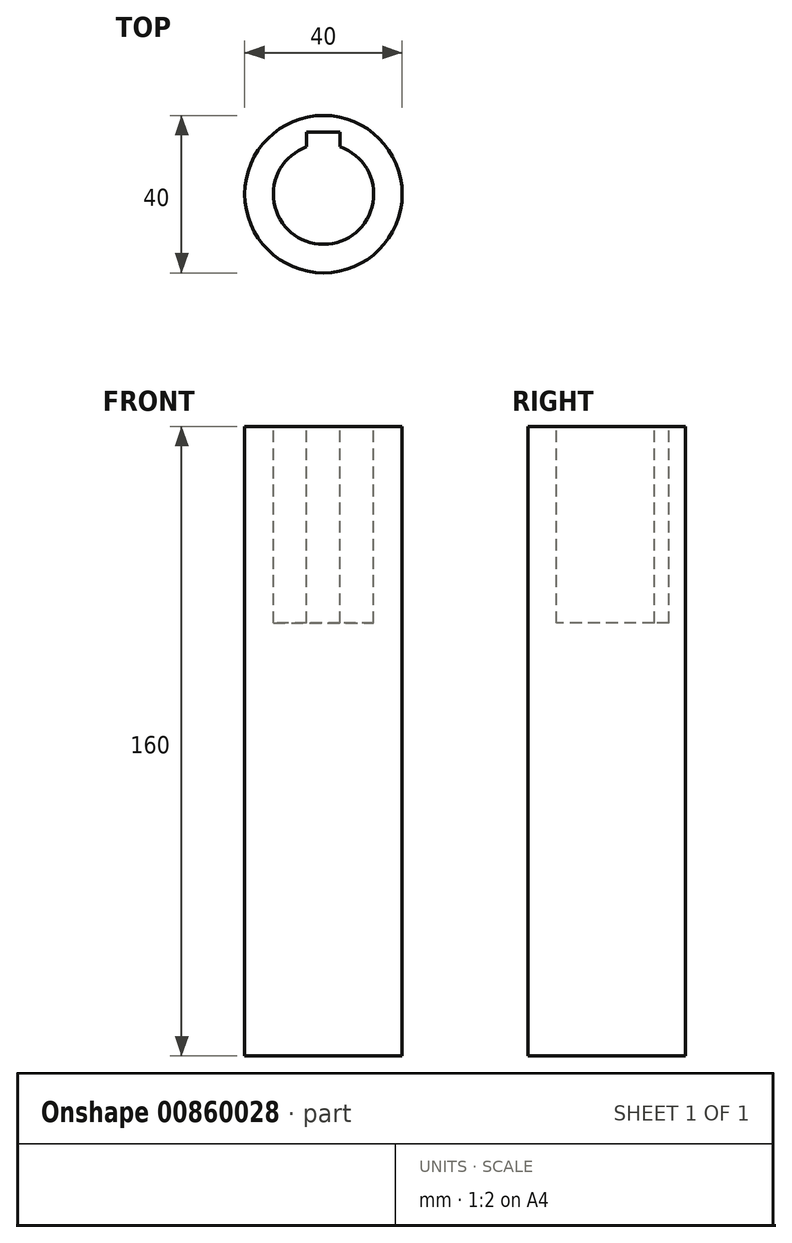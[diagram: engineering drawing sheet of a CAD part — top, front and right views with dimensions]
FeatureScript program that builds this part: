
annotation { "Feature Type Name" : "Feature", "Feature Type Description" : "" }
export const myFeature = defineFeature(function(context is Context, id is Id, definition is map)
    precondition{}
    {
        {
            var Q0;
            Q0=qCreatedBy(makeId("Top.planeOp"),FACE);
            var sketch = newSketch(context, id + "F0", { "sketchPlane" : qUnion([Q0])});
            skCircle(sketch, "E0", {"center": v(0, 0) * mm, "radius": 20 * mm});
            skSolve(sketch);
        }
        {
            var Q0;
            Q0 = qSketchRegion(id + "F0", true);
            extrude(context, id + "F1", {"entities" : qUnion([Q0]), "depth" : 160 * mm, "offsetDistance" : 25 * mm});
        }
        {
            var Q0;
            Q0=makeQuery(id+"F1.opExtrude","CAP_FACE",FACE,{"disambiguationData":[OSD([sQuery(id+"F0.wireOp",EDGE,"E0")])],"isStart":false});
            var sketch = newSketch(context, id + "F2", { "sketchPlane" : qUnion([Q0])});
            skCircle(sketch, "E1", {"center": v(0, 0) * mm, "radius": 12.75 * mm});
            skLineSegment(sketch, "E2.bottom", {"start": v(4.25, 15.75) * mm, "end": v(-4.25, 15.75) * mm});
            skLineSegment(sketch, "E2.top", {"start": v(4.25, 9.75) * mm, "end": v(-4.25, 9.75) * mm});
            skLineSegment(sketch, "E2.left", {"start": v(4.25, 15.75) * mm, "end": v(4.25, 9.75) * mm});
            skLineSegment(sketch, "E2.right", {"start": v(-4.25, 15.75) * mm, "end": v(-4.25, 9.75) * mm});
            skPoint(sketch, "E2.middle", {"position": v(0, 12.75) * mm});
            skSolve(sketch);
        }
        {
            var Q0;
            Q0 = qSketchRegion(id + "F2", true);
            extrude(context, id + "F3", {"entities" : qUnion([Q0]), "operationType" : NewBodyOperationType.REMOVE, "oppositeDirection" : true, "depth" : 50 * mm, "offsetDistance" : 25 * mm});
        }
    });
